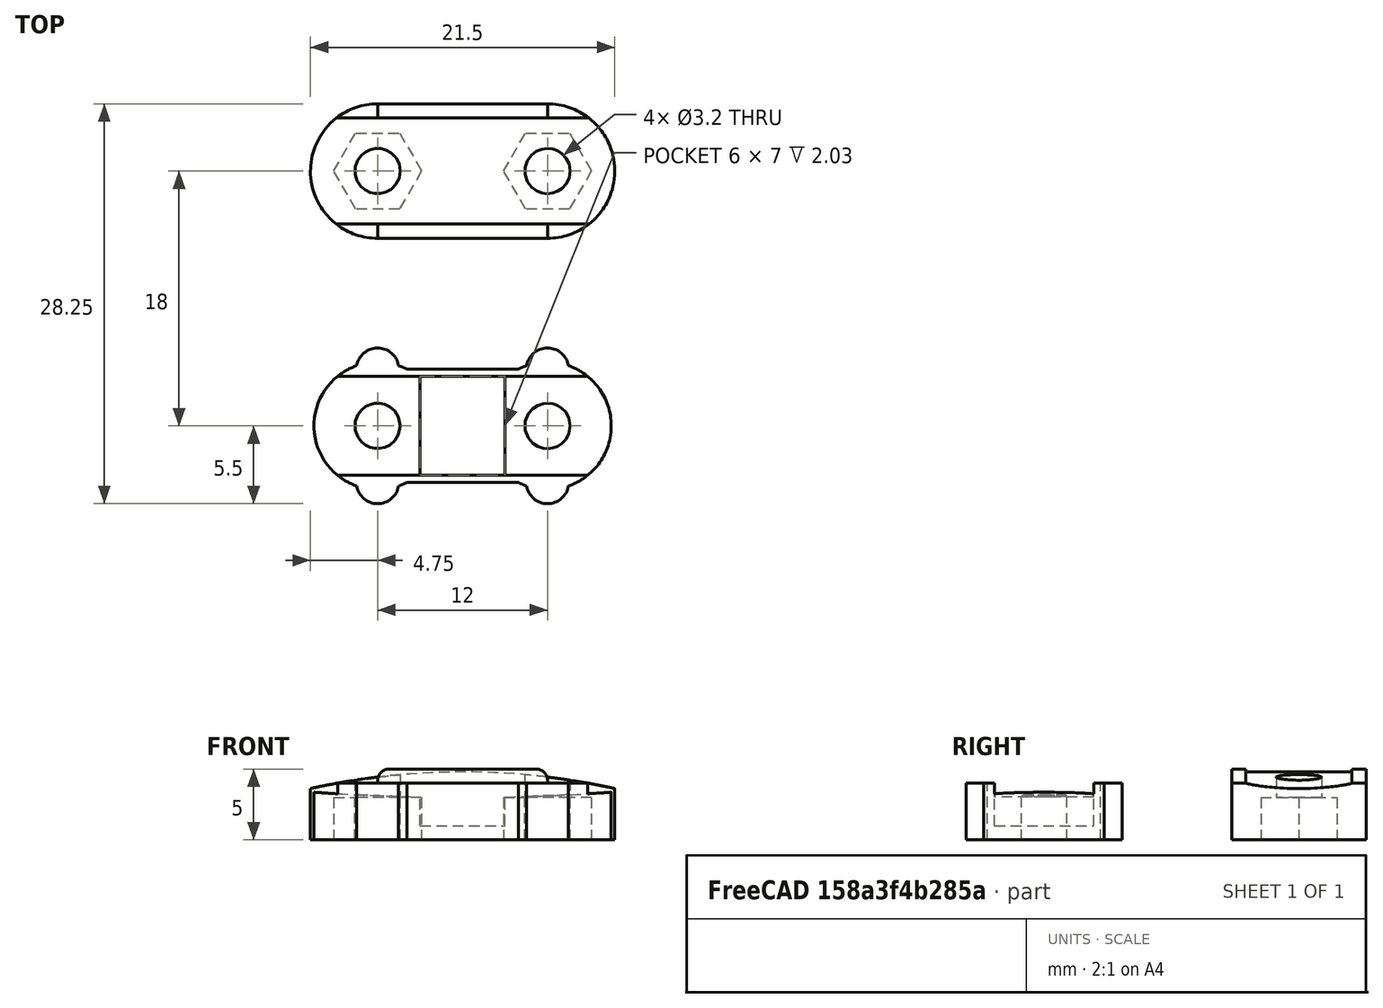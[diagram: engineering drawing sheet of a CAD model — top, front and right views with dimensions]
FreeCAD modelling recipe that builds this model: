
FCSTD DOCUMENT  (FreeCAD 0.15R3876 (Git))
Label: leafspring-mounts
License: CC-BY 3.0
LicenseURL: http://creativecommons.org/licenses/by/3.0/
objects: Part::Cylinder×16, Part::Box×14, Part::Cut×12, Part::MultiFuse×10, Part::Extrusion×2, Part::RegularPolygon×1, Part::Feature×1, Part::Fillet×1
note: 57 computed .brp shape members not serialized (recipe doc carries the construction recipe); baked Part::Feature solids carry a one-line shape summary decoded from their .brp

FEATURE [Part::RegularPolygon] RegularPolygon  label="Regular polygon"
  Circumradius = 3.1
  Polygon = 6
FEATURE [Part::Feature] Face
  shape: bbox 6.2 x 5.369 x 2e-07 mm, 1 faces, 0 solids (baked)
FEATURE [Part::Extrusion] Extrude
  Base = -> Face
  Dir = (0,0,3)
  Placement = pos=(12,-18,1) rot=(0,0,1;0rad)
  Solid = false
FEATURE [Part::Cylinder] Cylinder
  Angle = 360
  Height = 4
  Radius = 4.5
FEATURE [Part::Cylinder] Cylinder001
  Angle = 360
  Height = 4
  Placement = pos=(12,0,0) rot=(0,0,1;0rad)
  Radius = 4.5
FEATURE [Part::Box] Box
  Height = 1
  Length = 12
  Placement = pos=(0,-4,0) rot=(0,0,1;0rad)
  Width = 8
FEATURE [Part::MultiFuse] Fusion
  Shapes = -> [Box,Cylinder001,Cylinder]
FEATURE [Part::Box] Box001
  Height = 4
  Length = 12
  Placement = pos=(0,-4,0) rot=(0,0,1;0rad)
  Width = 1
FEATURE [Part::Box] Box002
  Height = 4
  Length = 12
  Placement = pos=(0,3,0) rot=(0,0,1;0rad)
  Width = 1
FEATURE [Part::Box] Box003
  Height = 1
  Length = 12
  Placement = pos=(0,3.5,3) rot=(0,0,1;0rad)
  Width = 0.5
FEATURE [Part::MultiFuse] Fusion001
  Shapes = -> [Fusion,Box002,Box001]
FEATURE [Part::Box] Box004
  Height = 1
  Length = 12
  Placement = pos=(0,-4,3) rot=(0,0,1;0rad)
  Width = 0.5
FEATURE [Part::MultiFuse] Fusion002
  Shapes = -> [Fusion001,Box003,Box004]
FEATURE [Part::Cylinder] Cylinder002
  Angle = 360
  Height = 4
  Radius = 1.5
FEATURE [Part::Box] Box005
  Height = 10
  Length = 10
  Placement = pos=(-5,0,0) rot=(0,0,1;0rad)
  Width = 10
FEATURE [Part::Cut] Cut
  Base = -> Cylinder002
  Placement = pos=(0,-4,0) rot=(0,0,1;0rad)
  Tool = -> Box005
FEATURE [Part::Cylinder] Cylinder003
  Angle = 360
  Height = 4
  Radius = 1.5
FEATURE [Part::Box] Box006
  Height = 10
  Length = 10
  Placement = pos=(-5,0,0) rot=(0,0,1;0rad)
  Width = 10
FEATURE [Part::Cut] Cut001
  Base = -> Cylinder003
  Placement = pos=(12,-4,0) rot=(0,0,1;0rad)
  Tool = -> Box006
FEATURE [Part::Cylinder] Cylinder004
  Angle = 360
  Height = 4
  Radius = 1.5
FEATURE [Part::Box] Box007
  Height = 10
  Length = 10
  Placement = pos=(-5,0,0) rot=(0,0,1;0rad)
  Width = 10
FEATURE [Part::Cut] Cut002
  Base = -> Cylinder004
  Placement = pos=(0,4,0) rot=(0,0,1;3.14159rad)
  Tool = -> Box007
FEATURE [Part::Cylinder] Cylinder005
  Angle = 360
  Height = 4
  Radius = 1.5
FEATURE [Part::Box] Box008
  Height = 10
  Length = 10
  Placement = pos=(-5,0,0) rot=(0,0,1;0rad)
  Width = 10
FEATURE [Part::Cut] Cut003
  Base = -> Cylinder005
  Placement = pos=(12,4,0) rot=(0,0,1;3.14159rad)
  Tool = -> Box008
FEATURE [Part::MultiFuse] Fusion003
  Shapes = -> [Fusion002,Cut003,Cut002,Cut001,Cut]
FEATURE [Part::Cylinder] Cylinder006
  Angle = 360
  Height = 10
  Radius = 1.6
FEATURE [Part::Cylinder] Cylinder007
  Angle = 360
  Height = 10
  Placement = pos=(12,0,0) rot=(0,0,1;0rad)
  Radius = 1.6
FEATURE [Part::MultiFuse] Fusion004
  Shapes = -> [Cylinder007,Cylinder006]
FEATURE [Part::Cut] Cut004
  Base = -> Fusion003
  Tool = -> Fusion004
FEATURE [Part::Cylinder] Cylinder008
  Angle = 360
  Height = 7
  Placement = pos=(6,3.5,153) rot=(1,0,0;1.5708rad)
  Radius = 150
FEATURE [Part::Cut] Cut005
  Base = -> Cut004
  Tool = -> Cylinder008
FEATURE [Part::Box] Box009
  Height = 3
  Length = 6
  Placement = pos=(3,-3.5,1) rot=(0,0,1;0rad)
  Width = 7
FEATURE [Part::Cut] Cut006
  Base = -> Cut005
  Tool = -> Box009
FEATURE [Part::Cylinder] Cylinder009
  Angle = 360
  Height = 4
  Placement = pos=(12,-18,0) rot=(0,0,1;0rad)
  Radius = 4.75
FEATURE [Part::Cylinder] Cylinder010
  Angle = 360
  Height = 4
  Placement = pos=(0,-18,0) rot=(0,0,1;0rad)
  Radius = 4.75
FEATURE [Part::Extrusion] Extrude001
  Base = -> Face
  Dir = (0,0,3)
  Placement = pos=(0,-18,1) rot=(0,0,1;0rad)
  Solid = false
FEATURE [Part::Box] Box010
  Height = 4
  Length = 12
  Placement = pos=(0,-22.75,0) rot=(0,0,1;0rad)
  Width = 9.5
FEATURE [Part::Box] Box011
  Height = 2
  Length = 12
  Placement = pos=(0,-22.75,-1) rot=(0,0,1;0rad)
  Width = 1
FEATURE [Part::Box] Box012
  Height = 2
  Length = 12
  Placement = pos=(0,-14.25,-1) rot=(0,0,1;0rad)
  Width = 1
FEATURE [Part::Cylinder] Cylinder011
  Angle = 360
  Height = 7.5
  Placement = pos=(6,-14.25,49.2) rot=(1,0,0;1.5708rad)
  Radius = 50
FEATURE [Part::Box] Box013
  Height = 300
  Length = 317
  Placement = pos=(-150,-22,0) rot=(0,0,1;0rad)
  Width = 10
FEATURE [Part::Cylinder] Cylinder012
  Angle = 360
  Height = 10
  Placement = pos=(0,-18,-9.2) rot=(0,0,1;0rad)
  Radius = 1.6
FEATURE [Part::Cylinder] Cylinder013
  Angle = 360
  Height = 10
  Placement = pos=(12,-18,-9.2) rot=(0,0,1;0rad)
  Radius = 1.6
FEATURE [Part::MultiFuse] Fusion007
  Placement = pos=(0,0,5) rot=(0,0,1;0rad)
  Shapes = -> [Cylinder013,Cylinder012]
FEATURE [Part::MultiFuse] Fusion008
  Shapes = -> [Box010,Box011,Box012]
FEATURE [Part::Fillet] Fillet
  Base = -> Fusion008
  Edges = 4 edges r=0.8: [Edge1,Edge3,Edge14,Edge15]
FEATURE [Part::MultiFuse] Fusion009
  Shapes = -> [Fillet,Cylinder009,Cylinder010]
FEATURE [Part::Cylinder] Cylinder014
  Angle = 360
  Height = 7.5
  Placement = pos=(6,-14.25,49.2) rot=(1,0,0;1.5708rad)
  Radius = 50
FEATURE [Part::Cylinder] Cylinder015
  Angle = 360
  Height = 7.5
  Placement = pos=(6,-14.25,49.2) rot=(1,0,0;1.5708rad)
  Radius = 51
FEATURE [Part::Cut] Cut008
  Base = -> Cylinder011
  Tool = -> Box013
FEATURE [Part::Cut] Cut009
  Base = -> Cylinder015
  Tool = -> Cylinder014
FEATURE [Part::MultiFuse] Fusion010
  Shapes = -> [Fusion009,Cut008]
FEATURE [Part::Cut] Cut010
  Base = -> Fusion010
  Tool = -> Cut009
FEATURE [Part::MultiFuse] Fusion011
  Shapes = -> [Extrude001,Extrude]
FEATURE [Part::Cut] Cut011
  Base = -> Cut010
  Tool = -> Fusion011
FEATURE [Part::Cut] Cut012
  Base = -> Cut011
  Placement = pos=(0,0,4) rot=(1,0,0;3.14159rad)
  Tool = -> Fusion007
